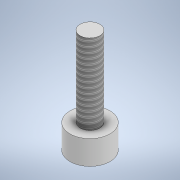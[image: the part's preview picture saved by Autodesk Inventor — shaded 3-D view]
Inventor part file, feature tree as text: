
AUTODESK INVENTOR PART (.ipt)
format: ipt  version: 2021 (Build 250183000, 183)  size: 108,032 bytes
history: native  units: in
note: dims shown in document units (in); Inventor stores cm internally (conversion verified against a paired STEP export)
features: extrude x2, sketch x2, other x1, thread x1
ambient origin geometry x8: Origin, YZ Plane, XZ Plane, XY Plane, X Axis, Y Axis, Z Axis, Center Point
bodies: Body1 (feature_tree)
feature tree (6):
  other  "Sólido1"
  extrude  "Extrusión1"  Depth=0.1181in TaperAngle=0.0deg
  extrude  "Extrusión2"  Depth=0.3937in TaperAngle=0.0deg
  thread  "Rosca1"  [1 undecoded]
  sketch  "Boceto1"  dims[d0=0.1969in d1=0.1181in d2=0.0in]
  sketch  "Boceto2"  dims[d3=0.0976in d4=0.3937in d5=0.0in d6=0.3937in d7=0.0in]
note: 1 required parameter value undecoded (feature->parameter linkage not recoverable at this tier; creation-order binding heuristic only, values carry confidence <= 0.55)
